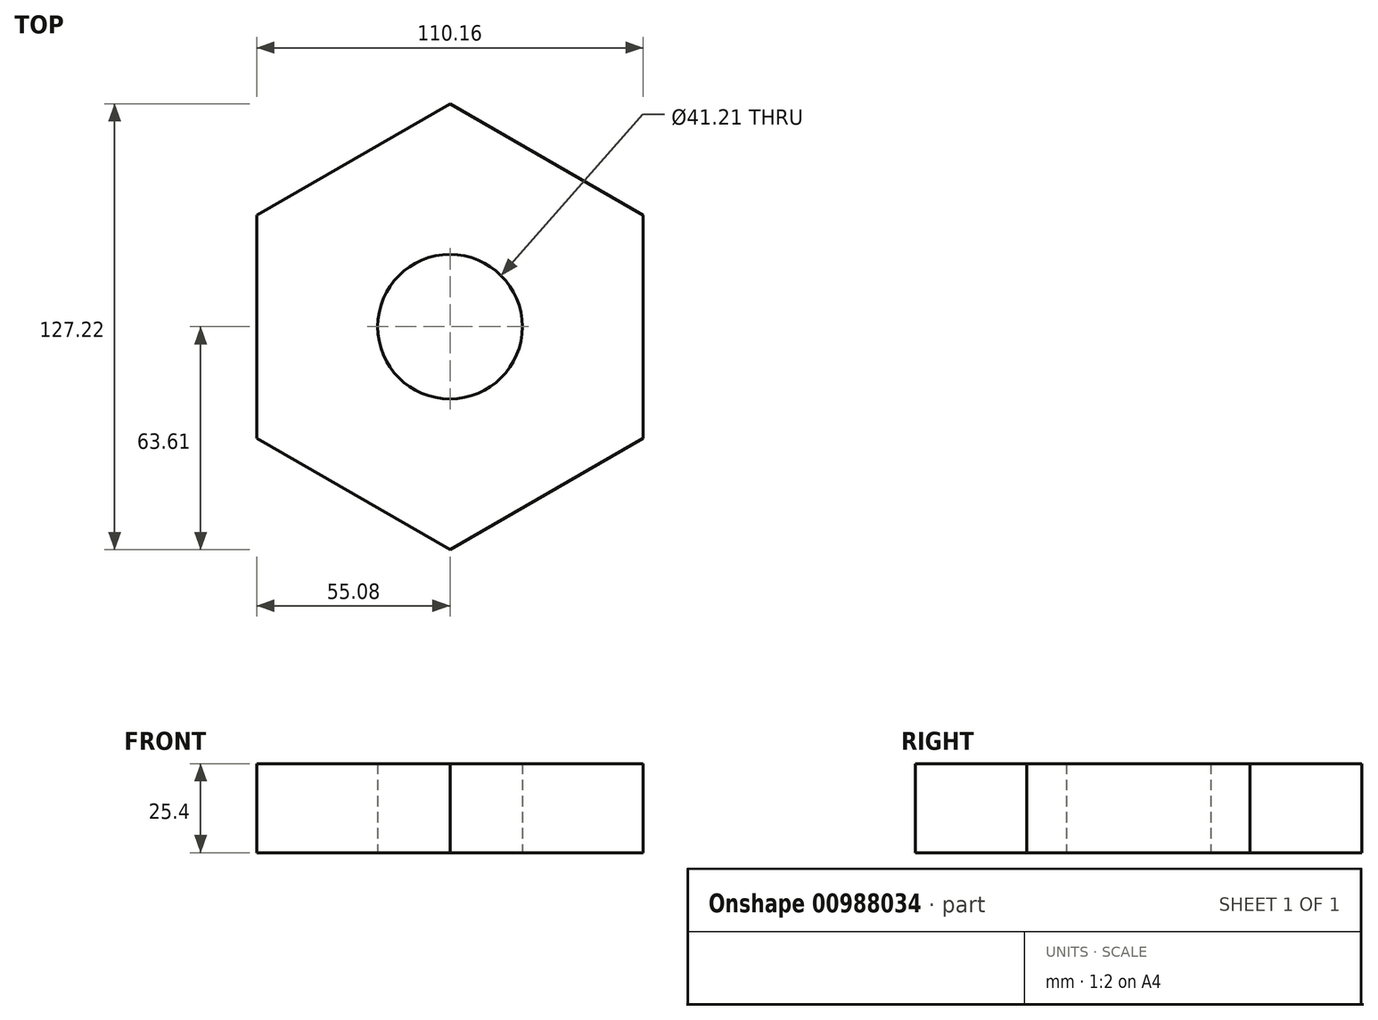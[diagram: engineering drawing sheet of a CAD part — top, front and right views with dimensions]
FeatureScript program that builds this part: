
annotation { "Feature Type Name" : "Feature", "Feature Type Description" : "" }
export const myFeature = defineFeature(function(context is Context, id is Id, definition is map)
    precondition{}
    {
        {
            var Q0;
            Q0=qCreatedBy(makeId("Top.planeOp"),FACE);
            var sketch = newSketch(context, id + "F0", { "sketchPlane" : qUnion([Q0])});
            skCircle(sketch, "E0.cCircle", {"center": v(0, 0) * mm, "radius": 55.08 * mm, "construction": true});
            skLineSegment(sketch, "E0.0", {"start": v(-55.08, -31.8) * mm, "end": v(-55.08, 31.8) * mm});
            skLineSegment(sketch, "E0.1", {"start": v(-55.08, 31.8) * mm, "end": v(0, 63.6) * mm});
            skLineSegment(sketch, "E0.2", {"start": v(0, 63.6) * mm, "end": v(55.08, 31.8) * mm});
            skLineSegment(sketch, "E0.3", {"start": v(55.08, 31.8) * mm, "end": v(55.08, -31.8) * mm});
            skLineSegment(sketch, "E0.4", {"start": v(55.08, -31.8) * mm, "end": v(0, -63.6) * mm});
            skLineSegment(sketch, "E0.5", {"start": v(0, -63.6) * mm, "end": v(-55.08, -31.8) * mm});
            skPoint(sketch, "E0.0.midPoint", {"position": v(-55.08, 0) * mm});
            skCircle(sketch, "E1", {"center": v(0, 0) * mm, "radius": 20.6 * mm});
            skSolve(sketch);
        }
        {
            var Q0;
            Q0 = qSketchRegion(id + "F0", true);
            extrude(context, id + "F1", {"entities" : qUnion([Q0]), "depth" : 25.4 * mm, "offsetDistance" : 25.4 * mm});
        }
    });
